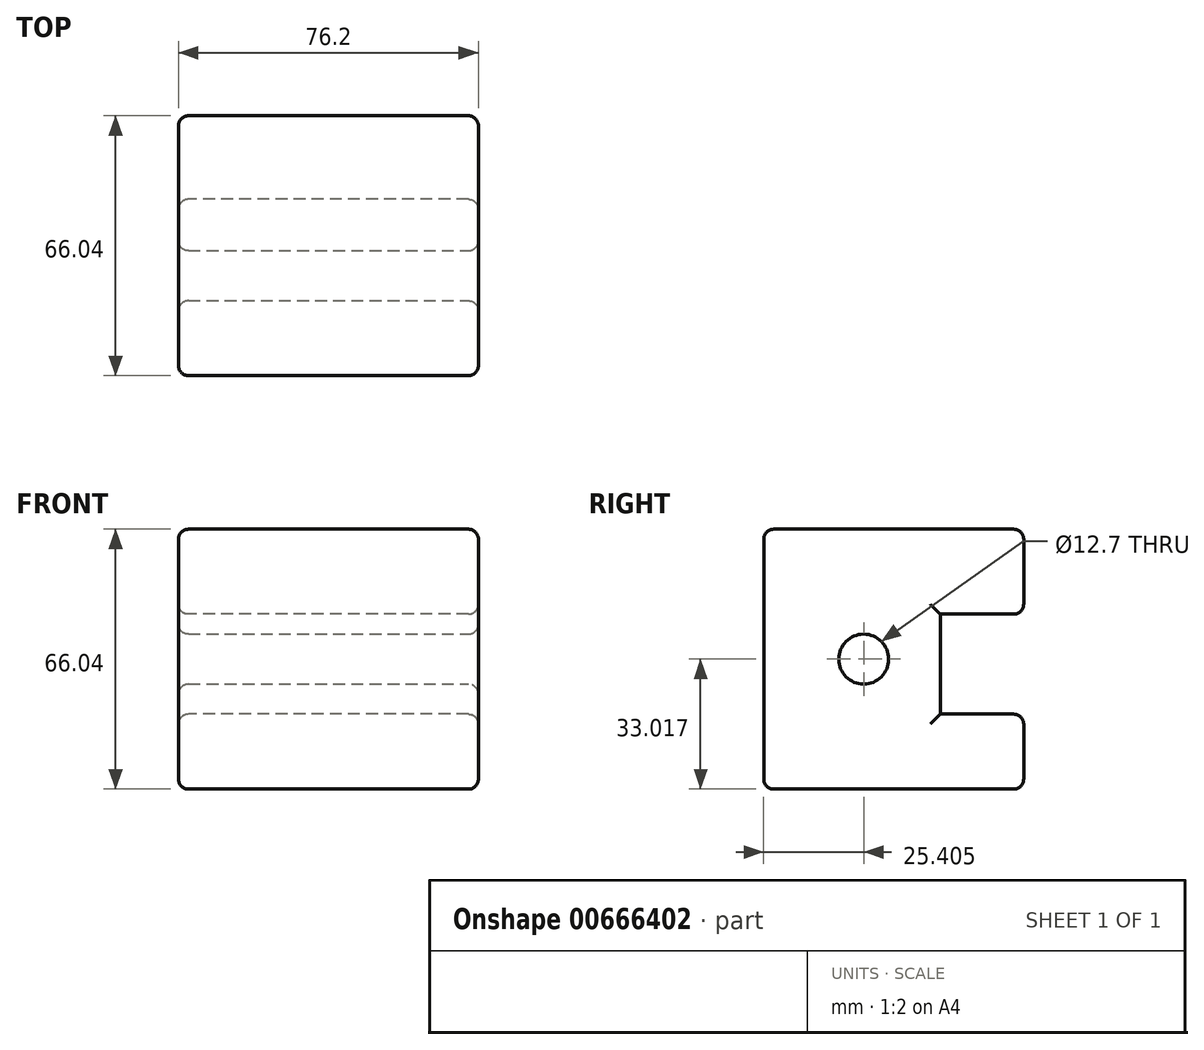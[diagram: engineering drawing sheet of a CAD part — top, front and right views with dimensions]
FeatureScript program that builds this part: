
annotation { "Feature Type Name" : "Feature", "Feature Type Description" : "" }
export const myFeature = defineFeature(function(context is Context, id is Id, definition is map)
    precondition{}
    {
        {
            var Q0;
            Q0=qCreatedBy(makeId("Right.planeOp"),FACE);
            var sketch = newSketch(context, id + "F0", { "sketchPlane" : qUnion([Q0])});
            skLineSegment(sketch, "E0.bottom", {"start": v(33.9, 36.94) * mm, "end": v(-32.14, 36.94) * mm});
            skLineSegment(sketch, "E0.top", {"start": v(33.9, -29.1) * mm, "end": v(-32.14, -29.1) * mm});
            skLineSegment(sketch, "E0.left", {"start": v(33.9, 36.94) * mm, "end": v(33.9, -29.1) * mm});
            skLineSegment(sketch, "E0.right", {"start": v(-32.14, 36.94) * mm, "end": v(-32.14, -29.1) * mm});
            skSolve(sketch);
        }
        {
            var Q0;
            Q0=qCreatedBy(makeId("Right.planeOp"),FACE);
            var sketch = newSketch(context, id + "F1", { "sketchPlane" : qUnion([Q0])});
            skLineSegment(sketch, "E1.bottom", {"start": v(50.8, -10.05) * mm, "end": v(12.7, -10.05) * mm});
            skLineSegment(sketch, "E1.top", {"start": v(50.8, 15.35) * mm, "end": v(12.7, 15.35) * mm});
            skLineSegment(sketch, "E1.left", {"start": v(50.8, -10.05) * mm, "end": v(50.8, 15.35) * mm});
            skLineSegment(sketch, "E1.right", {"start": v(12.7, -10.05) * mm, "end": v(12.7, 15.35) * mm});
            skSolve(sketch);
        }
        {
            var Q0;
            Q0 = qSketchRegion(id + "F0", true);
            extrude(context, id + "F2", {"entities" : qUnion([Q0]), "depth" : 76.2 * mm, "offsetDistance" : 25.4 * mm});
        }
        {
            var Q0;
            Q0 = qSketchRegion(id + "F1", true);
            extrude(context, id + "F3", {"entities" : qUnion([Q0]), "operationType" : NewBodyOperationType.REMOVE, "depth" : 76.2 * mm, "offsetDistance" : 25.4 * mm});
        }
        {
            var Q0;
            Q0=makeQuery(id+"F2.opExtrude","CAP_FACE",FACE,{"disambiguationData":[OSD([sQuery(id+"F0.wireOp",EDGE,"E0.bottom"),sQuery(id+"F0.wireOp",EDGE,"E0.top"),sQuery(id+"F0.wireOp",EDGE,"E0.left"),sQuery(id+"F0.wireOp",EDGE,"E0.right")])],"isStart":false});
            var sketch = newSketch(context, id + "F4", { "sketchPlane" : qUnion([Q0])});
            skCircle(sketch, "E2", {"center": v(-6.74, 3.92) * mm, "radius": 6.35 * mm});
            skSolve(sketch);
        }
        {
            var Q0;
            Q0 = qSketchRegion(id + "F4", true);
            extrude(context, id + "F5", {"entities" : qUnion([Q0]), "operationType" : NewBodyOperationType.REMOVE, "oppositeDirection" : true, "depth" : 101.6 * mm, "offsetDistance" : 25.4 * mm});
        }
        {
            var Q0;
            {var subQ0=sQuery(id+"F0.wireOp",EDGE,"E0.bottom");var subQ1=sQuery(id+"F0.wireOp",EDGE,"E0.left");Q0=makeQuery(id+"F3.boolean.opBoolean","SPLIT",EDGE,{"disambiguationData":[TD([makeQuery(id+"F2.opExtrude","SWEPT_FACE",FACE,{"disambiguationData":[OSD([subQ0])]})])],"derivedFrom":makeQuery(id+"F2.opExtrude","CAP_EDGE",EDGE,{"disambiguationData":[OSD([subQ1])],"isStart":true})});}
            var Q1;
            Q1=makeQuery(id+"F2.opExtrude","CAP_EDGE",EDGE,{"disambiguationData":[OSD([sQuery(id+"F0.wireOp",EDGE,"E0.bottom")])],"isStart":true});
            var Q2;
            Q2=makeQuery(id+"F2.opExtrude","CAP_FACE",FACE,{"disambiguationData":[OSD([sQuery(id+"F0.wireOp",EDGE,"E0.bottom"),sQuery(id+"F0.wireOp",EDGE,"E0.top"),sQuery(id+"F0.wireOp",EDGE,"E0.left"),sQuery(id+"F0.wireOp",EDGE,"E0.right")])],"isStart":true});
            var Q3;
            Q3=makeQuery(id+"F2.opExtrude","CAP_FACE",FACE,{"disambiguationData":[OSD([sQuery(id+"F0.wireOp",EDGE,"E0.bottom"),sQuery(id+"F0.wireOp",EDGE,"E0.top"),sQuery(id+"F0.wireOp",EDGE,"E0.left"),sQuery(id+"F0.wireOp",EDGE,"E0.right")])],"isStart":false});
            var Q4;
            {var subQ0=sQuery(id+"F0.wireOp",EDGE,"E0.bottom");var subQ2=sQuery(id+"F0.wireOp",EDGE,"E0.left");Q4=makeQuery(id+"F3.boolean.opBoolean","SPLIT",FACE,{"disambiguationData":[TD([makeQuery(id+"F2.opExtrude","SWEPT_FACE",FACE,{"disambiguationData":[OSD([subQ0])]})])],"derivedFrom":makeQuery(id+"F2.opExtrude","SWEPT_FACE",FACE,{"disambiguationData":[OSD([subQ2])]})});}
            var Q5;
            {var subQ1=sQuery(id+"F0.wireOp",EDGE,"E0.left");var subQ2=sQuery(id+"F0.wireOp",EDGE,"E0.top");Q5=makeQuery(id+"F3.boolean.opBoolean","SPLIT",FACE,{"disambiguationData":[TD([makeQuery(id+"F2.opExtrude","SWEPT_FACE",FACE,{"disambiguationData":[OSD([subQ2])]})])],"derivedFrom":makeQuery(id+"F2.opExtrude","SWEPT_FACE",FACE,{"disambiguationData":[OSD([subQ1])]})});}
            var Q6;
            Q6=makeQuery(id+"F2.opExtrude","SWEPT_FACE",FACE,{"disambiguationData":[OSD([sQuery(id+"F0.wireOp",EDGE,"E0.top")])]});
            var Q7;
            Q7=makeQuery(id+"F2.opExtrude","SWEPT_FACE",FACE,{"disambiguationData":[OSD([sQuery(id+"F0.wireOp",EDGE,"E0.bottom")])]});
            fillet(context, id + "F6", {"entities" : qUnion([Q0, Q1, Q2, Q3, Q4, Q5, Q6, Q7]), "radius" : 2.54 * mm, "tangentPropagation" : true, "allowEdgeOverflow" : false});
        }
    });
